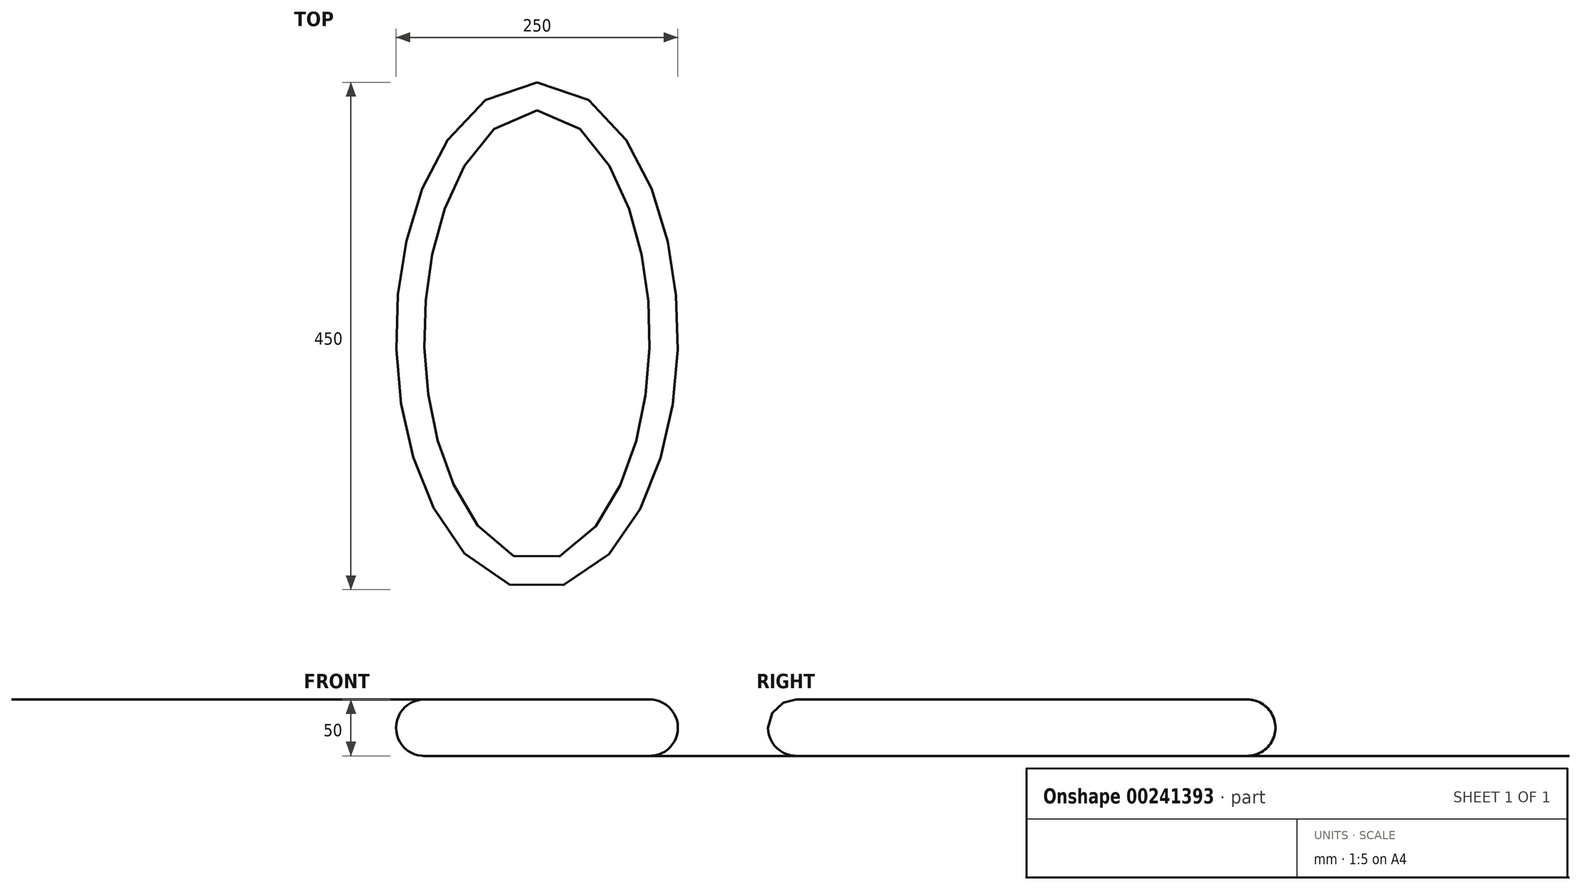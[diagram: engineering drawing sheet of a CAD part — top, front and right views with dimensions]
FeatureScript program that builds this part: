
annotation { "Feature Type Name" : "Feature", "Feature Type Description" : "" }
export const myFeature = defineFeature(function(context is Context, id is Id, definition is map)
    precondition{}
    {
        {
            var Q0;
            Q0=qCreatedBy(makeId("Top.planeOp"),FACE);
            var sketch = newSketch(context, id + "F0", { "sketchPlane" : qUnion([Q0])});
            skEllipse(sketch, "E0", {"center": v(0, 0) * mm, "majorRadius": 225 * mm, "minorRadius": 125 * mm, "majorAxis": v(0, 1)});
            skSolve(sketch);
        }
        {
            var Q0;
            Q0=makeQuery(id+"F0.imprint","IMPRINT",FACE,{"disambiguationData":[TD([[makeQuery(id+"F0.imprint","IMPRINT",EDGE,{"derivedFrom":sQuery(id+"F0.wireOp",EDGE,"E0")}),1.0]])]});
            extrude(context, id + "F1", {"entities" : qUnion([Q0]), "depth" : 50 * mm});
        }
        {
            var Q0;
            Q0=makeQuery(id+"F1.opExtrude","CAP_EDGE",EDGE,{"disambiguationData":[OSD([sQuery(id+"F0.wireOp",EDGE,"E0")])],"isStart":false});
            var Q1;
            Q1=makeQuery(id+"F1.opExtrude","CAP_EDGE",EDGE,{"disambiguationData":[OSD([sQuery(id+"F0.wireOp",EDGE,"E0")])],"isStart":true});
            fillet(context, id + "F2", {"entities" : qUnion([Q0, Q1]), "radius" : 25 * mm, "tangentPropagation" : true, "allowEdgeOverflow" : false});
        }
    });
